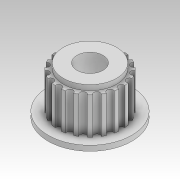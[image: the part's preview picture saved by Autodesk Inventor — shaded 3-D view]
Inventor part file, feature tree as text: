
AUTODESK INVENTOR PART (.ipt)
format: ipt  version: 2020 (Build 240168000, 168)  size: 210,432 bytes
history: native  units: mm
features: sketch x3, extrude x2, pattern_circular x2, revolve x1
ambient origin geometry x8: Origin, YZ Plane, XZ Plane, XY Plane, X Axis, Y Axis, Z Axis, Center Point
bodies: Solid1 (feature_tree)
feature tree (8):
  revolve  "Revolution1"  [1 undecoded]
  extrude  "Extrusion1"  Depth=6.11mm
  pattern_circular  "Circular Pattern1"  [2 undecoded]
  extrude  "Extrusion2"  TaperAngle=90.0deg  [1 undecoded]
  pattern_circular  "Circular Pattern2"  [2 undecoded]
  sketch  "Sketch1"  dims[d0=7.0mm d1=1.0mm]
  sketch  "Sketch2"  dims[d2=8.0mm d3=6.11mm]
  sketch  "Sketch3"  dims[d5=1.0mm d6=1.0mm d7=90.0deg d8=1.2mm d9=6.0mm d10=10.0mm d11=0.0mm d12=200.0mm d13=360.0deg d15=2.5mm d16=2.5mm d17=10.0mm d18=0.0mm d19=20.0mm d20=90.0deg]
note: 6 required parameter values undecoded (feature->parameter linkage not recoverable at this tier; creation-order binding heuristic only, values carry confidence <= 0.55)